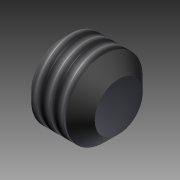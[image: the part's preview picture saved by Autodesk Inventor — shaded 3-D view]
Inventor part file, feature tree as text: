
AUTODESK INVENTOR PART (.ipt)
format: ipt  version: 2016 (Build 200138000, 138)  size: 138,240 bytes
history: native  units: mm
features: other x7, sketch x3, revolve x2, thread x1, extrude x1
ambient origin geometry x8: Origin, YZ Plane, XZ Plane, XY Plane, X Axis, Y Axis, Z Axis, Center Point
bodies: Solid1 (feature_tree)
feature tree (14):
  revolve  "Revolution1"  [1 undecoded]
  thread  "Thread1"  [1 undecoded]
  extrude  "Extrusion1"  TaperAngle=0.0deg  [1 undecoded]
  revolve  "Revolution2"  [1 undecoded]
  other  "CP_XY"
  other  "CP_YZ"
  other  "CP_ZX"
  other  "CP_X"
  other  "CP_Y"
  other  "CP_Z"
  other  "CP_Center"
  sketch  "Sketch_1"  dims[d0=360.0deg d1=1.8205mm d2=0.0mm d3=1.5mm d4=0.0mm]
  sketch  "Sketch_2"  dims[d5=360.0deg d6=0.0mm]
  sketch  "Sketch_3"
note: 4 required parameter values undecoded (feature->parameter linkage not recoverable at this tier; creation-order binding heuristic only, values carry confidence <= 0.55)